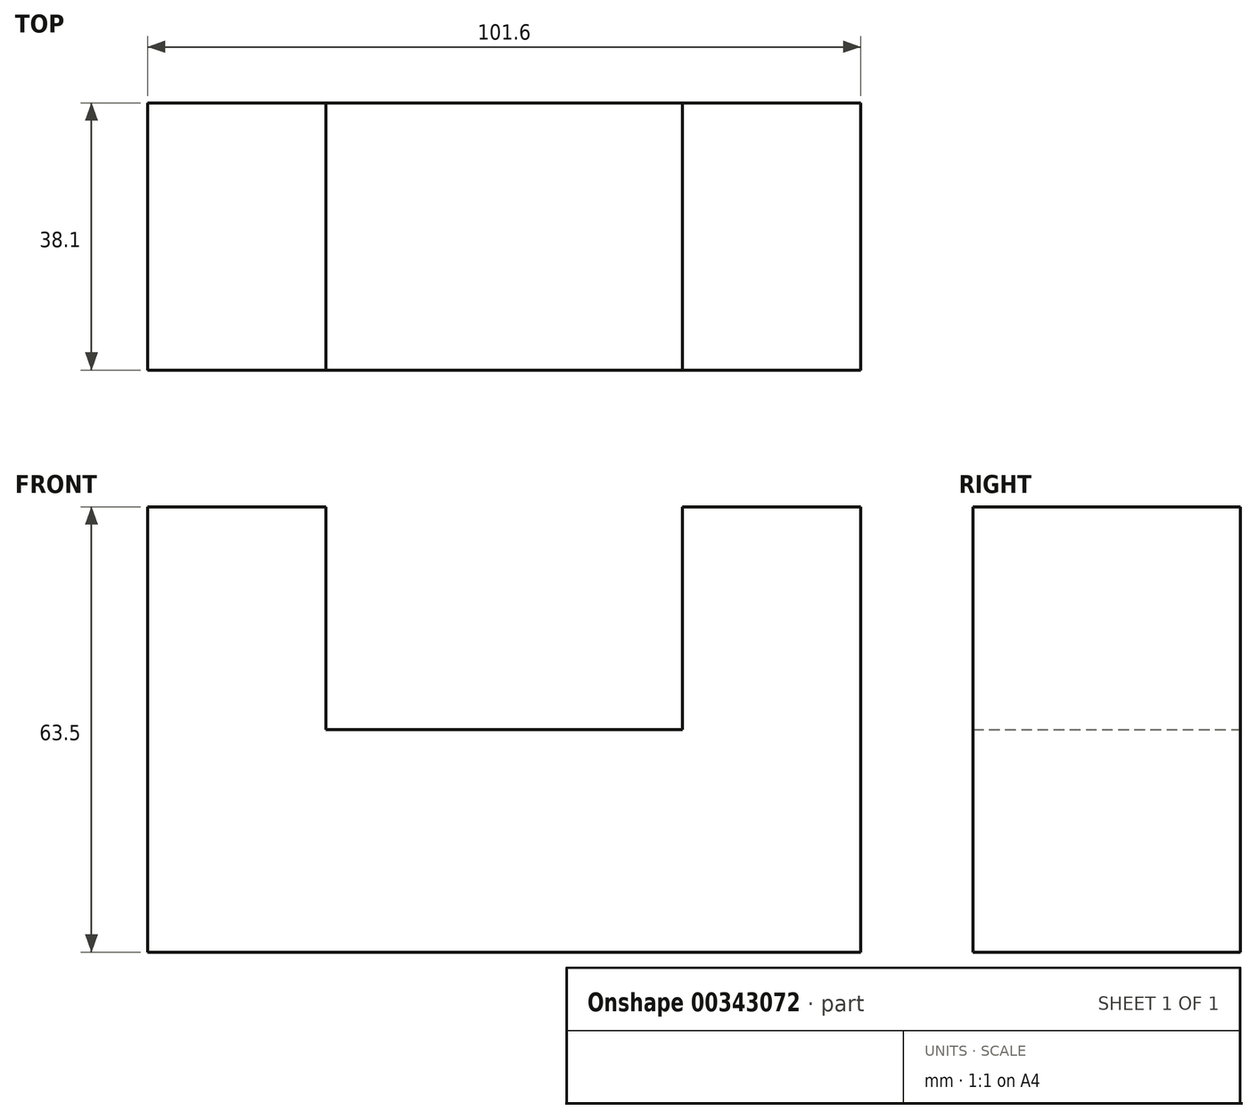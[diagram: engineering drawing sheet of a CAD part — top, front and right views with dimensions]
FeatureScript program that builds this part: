
annotation { "Feature Type Name" : "Feature", "Feature Type Description" : "" }
export const myFeature = defineFeature(function(context is Context, id is Id, definition is map)
    precondition{}
    {
        {
            var Q0;
            Q0=qCreatedBy(makeId("Front.planeOp"),FACE);
            var sketch = newSketch(context, id + "F0", { "sketchPlane" : qUnion([Q0])});
            skLineSegment(sketch, "E0", {"start": v(-46.34, -63.5) * mm, "end": v(55.26, -63.5) * mm});
            skLineSegment(sketch, "E1", {"start": v(55.26, -63.5) * mm, "end": v(55.26, 0) * mm});
            skLineSegment(sketch, "E2", {"start": v(55.26, 0) * mm, "end": v(29.86, 0) * mm});
            skLineSegment(sketch, "E3", {"start": v(29.86, 0) * mm, "end": v(29.86, -31.75) * mm});
            skLineSegment(sketch, "E4", {"start": v(-46.34, -63.5) * mm, "end": v(-46.34, 0) * mm});
            skLineSegment(sketch, "E5", {"start": v(-46.34, 0) * mm, "end": v(-20.94, 0) * mm});
            skLineSegment(sketch, "E6", {"start": v(-20.94, 0) * mm, "end": v(-20.94, -31.75) * mm});
            skLineSegment(sketch, "E7", {"start": v(-20.94, -31.75) * mm, "end": v(29.86, -31.75) * mm});
            skSolve(sketch);
        }
        {
            var Q0;
            Q0 = qSketchRegion(id + "F0", true);
            extrude(context, id + "F1", {"entities" : qUnion([Q0]), "depth" : 38.1 * mm});
        }
    });
